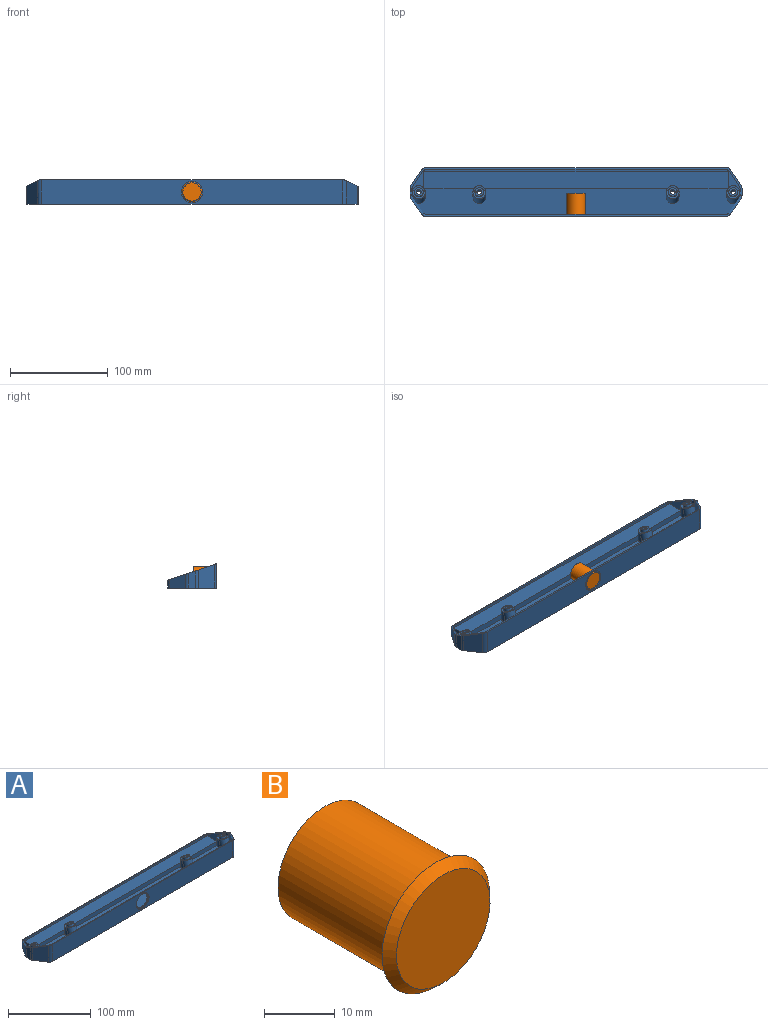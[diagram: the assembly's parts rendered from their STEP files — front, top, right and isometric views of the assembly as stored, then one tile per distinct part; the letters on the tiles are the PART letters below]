
ASSEMBLY  parts=2 mates=1
PART A: 95 faces, bbox 340x50x27.4 mm
  f0: plane 9x8.52mm, normal (0,0.32,0.95), area 44mm2, adj f33,f79
  f1: plane 9x8.52mm, normal (0,0.32,0.95), area 44mm2, adj f32,f78
  f2: plane 9x8.52mm, normal (0,0.32,0.95), area 44mm2, adj f31,f77
  f3: plane 340x50mm, normal (0,0.32,0.95), area 1550.9mm2, adj f13,f14,f16,f17,f18,f19,f20,f21
  f4: plane 340x50mm, normal (0,0,-1), area 12000.4mm2, adj f6,f8,f10,f12,f13,f14,f16,f17
  f5: plane 9x6.8mm, normal (0,-0.32,-0.95), area 34.8mm2, adj f6,f33,f40
  f6: cylinder r=4.5mm len=15.65mm, axis (0,-0.32,-0.95), area 237.3mm2, adj f4,f5,f40,f41
  f7: plane 9x6.8mm, normal (0,-0.32,-0.95), area 34.8mm2, adj f8,f32,f38
  f8: cylinder r=4.5mm len=15.65mm, axis (0,-0.32,-0.95), area 237.3mm2, adj f4,f7,f38,f39
  f9: plane 9x6.8mm, normal (0,-0.32,-0.95), area 34.8mm2, adj f10,f31,f36
  f10: cylinder r=4.5mm len=15.65mm, axis (0,-0.32,-0.95), area 237.3mm2, adj f4,f9,f36,f37
  f11: plane 9x6.8mm, normal (0,-0.32,-0.95), area 34.8mm2, adj f12,f30,f34
  f12: cylinder r=4.5mm len=15.65mm, axis (0,-0.32,-0.95), area 237.3mm2, adj f4,f11,f34,f35
  f13: plane 307.69x25mm, normal (0,-1,0), area 7312mm2, adj f3,f4,f20,f28,f94
  f14: plane 307.69x8mm, normal (0,1,0), area 2461.5mm2, adj f3,f4,f22,f26
  f15: plane 9x8.52mm, normal (0,0.32,0.95), area 44mm2, adj f30,f76
  f16: plane 17.68x6.94mm, normal (1,0,0), area 114.5mm2, adj f3,f4,f24,f27
  f17: plane 17.68x6.94mm, normal (-1,0,0), area 114.5mm2, adj f3,f4,f18,f21
  f18: cylinder r=5mm len=18.63mm, axis (0,0,-1), area 53.9mm2, adj f3,f4,f17,f19
  f19: plane 24.25x16.53mm, normal (-0.83,-0.56,0), area 427.6mm2, adj f3,f4,f18,f20
  f20: cylinder r=5mm len=25mm, axis (0,0,-1), area 120.9mm2, adj f3,f4,f13,f19
  f21: cylinder r=5mm len=15.32mm, axis (0,0,-1), area 44mm2, adj f3,f4,f17,f23
  f22: cylinder r=5mm len=8.75mm, axis (0,0,-1), area 40.3mm2, adj f3,f4,f14,f23
  f23: plane 16.53x14.37mm, normal (-0.83,0.56,0), area 230.5mm2, adj f3,f4,f21,f22
  f24: cylinder r=5mm len=15.32mm, axis (0,0,-1), area 44mm2, adj f3,f4,f16,f25
  f25: plane 16.53x14.37mm, normal (0.83,0.56,0), area 230.5mm2, adj f3,f4,f24,f26
  f26: cylinder r=5mm len=8.75mm, axis (0,0,-1), area 40.3mm2, adj f3,f4,f14,f25
  f27: cylinder r=5mm len=18.63mm, axis (0,0,-1), area 53.9mm2, adj f3,f4,f16,f29
  f28: cylinder r=5mm len=25mm, axis (0,0,-1), area 120.9mm2, adj f3,f4,f13,f29
  f29: plane 24.25x16.53mm, normal (0.83,-0.56,0), area 427.6mm2, adj f3,f4,f27,f28
  f30: cylinder r=2.5mm len=6.31mm, axis (0,-0.32,-0.95), area 76.9mm2, adj f11,f15
  f31: cylinder r=2.5mm len=6.31mm, axis (0,-0.32,-0.95), area 76.9mm2, adj f2,f9
  f32: cylinder r=2.5mm len=6.31mm, axis (0,-0.32,-0.95), area 76.9mm2, adj f1,f7
  f33: cylinder r=2.5mm len=6.31mm, axis (0,-0.32,-0.95), area 76.9mm2, adj f0,f5
  f34: plane 9x5.41mm, normal (0,0,-1), area 24.6mm2, adj f11,f12,f35
  f35: cylinder r=4.5mm len=11mm, axis (0,0,-1), area 197.1mm2, adj f4,f12,f34
  f36: plane 9x5.41mm, normal (0,0,-1), area 24.6mm2, adj f9,f10,f37
  f37: cylinder r=4.5mm len=11mm, axis (0,0,-1), area 197.1mm2, adj f4,f10,f36
  f38: plane 9x5.41mm, normal (0,0,-1), area 24.6mm2, adj f7,f8,f39
  f39: cylinder r=4.5mm len=11mm, axis (0,0,-1), area 197.1mm2, adj f4,f8,f38
  f40: plane 9x5.41mm, normal (0,0,-1), area 24.6mm2, adj f5,f6,f41
  f41: cylinder r=4.5mm len=11mm, axis (0,0,-1), area 197.1mm2, adj f4,f6,f40
  f42: plane 308x6mm, normal (0,1,0), area 1848mm2, adj f4,f43,f45,f46
  f43: plane 13x6mm, normal (1,0,0), area 78mm2, adj f4,f42,f44,f46
  f44: plane 308x6mm, normal (0,-1,0), area 1848mm2, adj f4,f43,f45,f46
  f45: plane 13x6mm, normal (-1,0,0), area 78mm2, adj f4,f42,f44,f46
  f46: plane 308x13mm, normal (0,0,-1), area 4004mm2, adj f42,f43,f44,f45
  f47: plane 312x17mm, normal (0,0,1), area 5268.2mm2, adj f48,f49,f81,f83,f85,f87,f88,f89
  f48: plane 51.75x6mm, normal (0,-1,0), area 310.5mm2, adj f47,f51,f81,f85
  f49: plane 187.75x6mm, normal (0,-1,0), area 1126.5mm2, adj f47,f51,f85,f87
  f50: plane 336.02x28.15mm, normal (0,0,1), area 823.1mm2, adj f57,f59,f61,f62,f63,f64,f67,f68
  f51: plane 326.6x27mm, normal (0,0,1), area 8110.2mm2, adj f48,f49,f53,f55,f57,f59,f60,f65
  f52: plane 13x8.38mm, normal (0,0.32,0.95), area 44.3mm2, adj f53,f79,f86
  f53: cylinder r=6.5mm len=16.72mm, axis (0,-0.32,-0.95), area 319.2mm2, adj f51,f52,f86,f87
  f54: plane 13x8.38mm, normal (0,0.32,0.95), area 44.3mm2, adj f55,f78,f84
  f55: cylinder r=6.5mm len=16.72mm, axis (0,-0.32,-0.95), area 319.2mm2, adj f51,f54,f84,f85
  f56: plane 13x8.38mm, normal (0,0.32,0.95), area 44.3mm2, adj f57,f77,f82
  f57: cylinder r=6.5mm len=16.71mm, axis (0,-0.32,-0.95), area 287.7mm2, adj f50,f51,f56,f73,f75,f82,f83
  f58: plane 13x8.38mm, normal (0,0.32,0.95), area 44.3mm2, adj f59,f76,f80
  f59: cylinder r=6.5mm len=16.71mm, axis (0,-0.32,-0.95), area 287.7mm2, adj f50,f51,f58,f64,f65,f80,f81
  f60: plane 307.69x22.32mm, normal (0,1,0), area 6584mm2, adj f3,f51,f66,f74,f92
  f61: plane 307.69x6.68mm, normal (0,-1,0), area 2055.3mm2, adj f3,f50,f68,f72
  f62: plane 15.68x6.94mm, normal (-1,0,0), area 100.6mm2, adj f3,f50,f70,f73
  f63: plane 15.68x6.94mm, normal (1,0,0), area 100.6mm2, adj f3,f50,f64,f67
  f64: cylinder r=3mm len=16.25mm, axis (0,0,-1), area 28.4mm2, adj f3,f50,f59,f63,f65
  f65: plane 21.87x16.53mm, normal (0.83,0.56,0), area 350.2mm2, adj f3,f51,f59,f64,f66
  f66: cylinder r=3mm len=22.32mm, axis (0,0,-1), area 65mm2, adj f3,f51,f60,f65
  f67: cylinder r=3mm len=13.32mm, axis (0,0,-1), area 23.2mm2, adj f3,f50,f63,f69
  f68: cylinder r=3mm len=7.13mm, axis (0,0,-1), area 20mm2, adj f3,f50,f61,f69
  f69: plane 16.53x12.75mm, normal (0.83,-0.56,0), area 198.2mm2, adj f3,f50,f67,f68
  f70: cylinder r=3mm len=13.32mm, axis (0,0,-1), area 23.2mm2, adj f3,f50,f62,f71
  f71: plane 16.53x12.75mm, normal (-0.83,-0.56,0), area 198.2mm2, adj f3,f50,f70,f72
  f72: cylinder r=3mm len=7.13mm, axis (0,0,-1), area 20mm2, adj f3,f50,f61,f71
  f73: cylinder r=3mm len=16.25mm, axis (0,0,-1), area 28.4mm2, adj f3,f50,f57,f62,f75
  f74: cylinder r=3mm len=22.32mm, axis (0,0,-1), area 65mm2, adj f3,f51,f60,f75
  f75: plane 21.87x16.53mm, normal (-0.83,0.56,0), area 350.2mm2, adj f3,f51,f57,f73,f74
  f76: cylinder r=4.5mm len=9.45mm, axis (0,-0.32,-0.95), area 77.5mm2, adj f15,f58,f80
  f77: cylinder r=4.5mm len=9.45mm, axis (0,-0.32,-0.95), area 77.5mm2, adj f2,f56,f82
  f78: cylinder r=4.5mm len=9.45mm, axis (0,-0.32,-0.95), area 77.5mm2, adj f1,f54,f84
  f79: cylinder r=4.5mm len=9.45mm, axis (0,-0.32,-0.95), area 77.5mm2, adj f0,f52,f86
  f80: plane 13.01x7.09mm, normal (0,0,1), area 37.9mm2, adj f58,f59,f76,f81
  f81: cylinder r=6.5mm len=13mm, axis (0,0,-1), area 256.6mm2, adj f47,f48,f50,f51,f59,f80,f89
  f82: plane 13.01x7.09mm, normal (0,0,1), area 37.9mm2, adj f56,f57,f77,f83
  f83: cylinder r=6.5mm len=13mm, axis (0,0,-1), area 256.6mm2, adj f47,f50,f51,f57,f82,f88,f91
  f84: plane 13.01x7.09mm, normal (0,0,1), area 37.9mm2, adj f54,f55,f78,f85
  f85: cylinder r=6.5mm len=13mm, axis (0,0,-1), area 187mm2, adj f47,f48,f49,f51,f55,f84
  f86: plane 13.01x7.09mm, normal (0,0,1), area 37.9mm2, adj f52,f53,f79,f87
  f87: cylinder r=6.5mm len=13mm, axis (0,0,-1), area 187mm2, adj f47,f49,f51,f53,f86,f88
  f88: plane 51.75x6mm, normal (0,-1,0), area 310.5mm2, adj f47,f51,f83,f87
  f89: plane 16.85x6mm, normal (-1,0,0), area 101.1mm2, adj f47,f50,f81,f90
  f90: plane 312x6mm, normal (0,1,0), area 1872mm2, adj f47,f50,f89,f91
  f91: plane 16.85x6mm, normal (1,0,0), area 101.1mm2, adj f47,f50,f83,f90
  f92: cylinder r=9.5mm len=19mm, axis (0,-1,0), area 59.7mm2, adj f60,f93
  f93: plane 22x22mm, normal (0,-1,0), area 96.6mm2, adj f92,f94
  f94: cylinder r=11mm len=22mm, axis (0,-1,0), area 69.1mm2, adj f13,f93
PART B: 5 faces, bbox 21.6x23.7x21.6 mm
  f0: plane 18.75x18.75mm, normal (0,-1,0), area 276.1mm2, adj f4
  f1: plane 18.75x18.75mm, normal (0,1,0), area 276.1mm2, adj f2
  f2: cylinder r=9.38mm len=22.24mm, axis (0,1,0), area 1310mm2, adj f1,f3
  f3: plane 21.55x21.55mm, normal (0,1,0), area 88.6mm2, adj f2,f4
  f4: cone r=9.38mm half-angle=43deg, axis (0,1,0), area 129.9mm2, adj f0,f3
PLACE A t=(-81.81,19.95,-40.69)mm
PLACE B t=(88.19,19.95,-28.19)mm
MATE fastened A.f92 <-> B.f2  axis (0,-1,0) through (88.19,19.95,-28.19)mm
